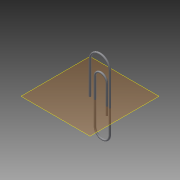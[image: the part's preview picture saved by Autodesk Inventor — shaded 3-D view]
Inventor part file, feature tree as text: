
AUTODESK INVENTOR PART (.ipt)
format: ipt  version: 2015 (Build 190159000, 159)  size: 100,864 bytes
history: native  units: in
note: dims shown in document units (in); Inventor stores cm internally (conversion verified against a paired STEP export)
features: sketch x2, plane x1, sweep x1
ambient origin geometry x8: Origin, YZ Plane, XZ Plane, XY Plane, X Axis, Y Axis, Z Axis, Center Point
bodies: Solid1 (feature_tree)
feature tree (4):
  sketch  "Sketch1"  dims[d0=0.0in d1=0.0in]
  plane  "Work Plane1"
  sweep  "Sweep1"
  sketch  "Sketch2"
